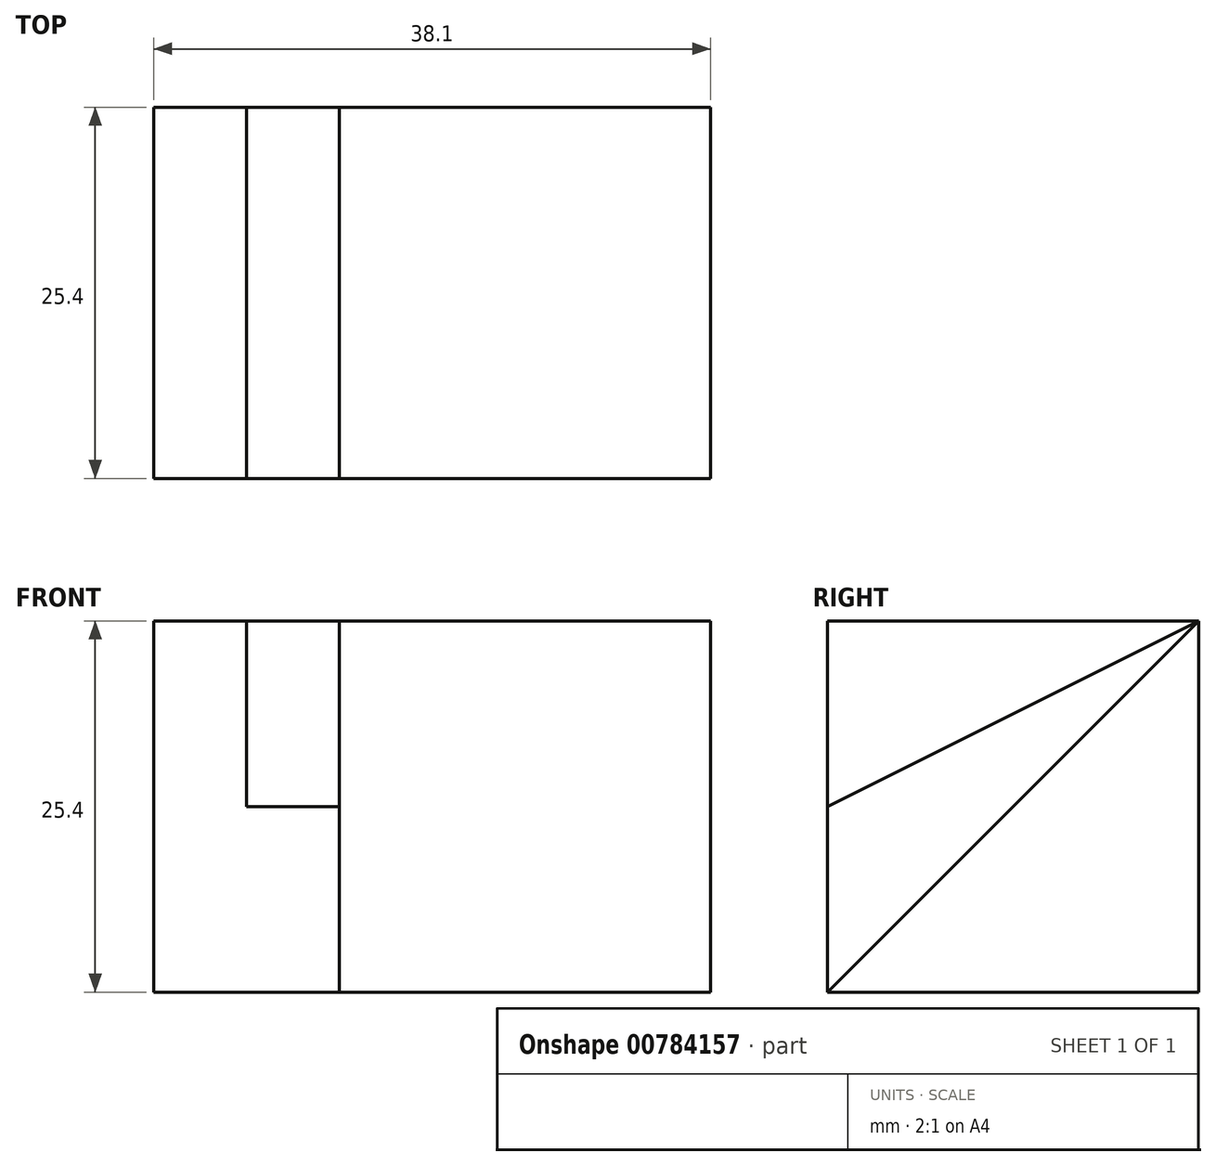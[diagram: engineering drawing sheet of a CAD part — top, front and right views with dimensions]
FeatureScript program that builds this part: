
annotation { "Feature Type Name" : "Feature", "Feature Type Description" : "" }
export const myFeature = defineFeature(function(context is Context, id is Id, definition is map)
    precondition{}
    {
        {
            var Q0;
            Q0=qCreatedBy(makeId("Front.planeOp"),FACE);
            var sketch = newSketch(context, id + "F0", { "sketchPlane" : qUnion([Q0])});
            skLineSegment(sketch, "E0", {"start": v(0, 0) * mm, "end": v(38.1, 0) * mm});
            skLineSegment(sketch, "E1", {"start": v(38.1, 0) * mm, "end": v(38.1, 25.4) * mm});
            skLineSegment(sketch, "E2", {"start": v(38.1, 25.4) * mm, "end": v(0, 25.4) * mm});
            skLineSegment(sketch, "E3", {"start": v(0, 25.4) * mm, "end": v(0, 0) * mm});
            skSolve(sketch);
        }
        {
            var Q0;
            Q0=makeQuery(id+"F0.imprint","IMPRINT",FACE,{"disambiguationData":[TD([[makeQuery(id+"F0.imprint","IMPRINT",EDGE,{"derivedFrom":sQuery(id+"F0.wireOp",EDGE,"E0")}),1.0]])]});
            extrude(context, id + "F1", {"entities" : qUnion([Q0]), "depth" : 25.4 * mm, "offsetDistance" : 25.4 * mm});
        }
        {
            var Q0;
            Q0=makeQuery(id+"F1.opExtrude","SWEPT_FACE",FACE,{"disambiguationData":[OSD([sQuery(id+"F0.wireOp",EDGE,"E1")])]});
            var sketch = newSketch(context, id + "F2", { "sketchPlane" : qUnion([Q0])});
            skLineSegment(sketch, "E4", {"start": v(0, 25.4) * mm, "end": v(-25.4, 0) * mm});
            skSolve(sketch);
        }
        {
            var Q0;
            Q0=makeQuery(id+"F2.imprint","IMPRINT",FACE,{"disambiguationData":[TD([[makeQuery(id+"F2.imprint","IMPRINT",EDGE,{"derivedFrom":sQuery(id+"F2.wireOp",EDGE,"E4")}),-1.0]])]});
            extrude(context, id + "F3", {"entities" : qUnion([Q0]), "operationType" : NewBodyOperationType.REMOVE, "oppositeDirection" : true, "depth" : 25.4 * mm, "offsetDistance" : 25.4 * mm});
        }
        {
            var Q0;
            Q0=makeQuery(id+"F1.opExtrude","CAP_FACE",FACE,{"disambiguationData":[OSD([sQuery(id+"F0.wireOp",EDGE,"E0"),sQuery(id+"F0.wireOp",EDGE,"E1"),sQuery(id+"F0.wireOp",EDGE,"E2"),sQuery(id+"F0.wireOp",EDGE,"E3")])],"isStart":false});
            var sketch = newSketch(context, id + "F4", { "sketchPlane" : qUnion([Q0])});
            skLineSegment(sketch, "E5", {"start": v(12.7, 0) * mm, "end": v(12.7, 12.7) * mm});
            skLineSegment(sketch, "E6", {"start": v(12.7, 12.7) * mm, "end": v(37.77, 50.75) * mm});
            skLineSegment(sketch, "E7", {"start": v(37.77, 50.75) * mm, "end": v(12.7, 25.4) * mm});
            skLineSegment(sketch, "E8", {"start": v(12.7, 25.4) * mm, "end": v(12.7, 12.7) * mm});
            skSolve(sketch);
        }
        {
            var Q0;
            Q0=makeQuery(id+"F4.imprint","IMPRINT",FACE,{"disambiguationData":[TD([[makeQuery(id+"F4.imprint","IMPRINT",EDGE,{"derivedFrom":sQuery(id+"F4.wireOp",EDGE,"E6")}),1.0]])]});
            extrude(context, id + "F5", {"entities" : qUnion([Q0]), "operationType" : NewBodyOperationType.REMOVE, "oppositeDirection" : true, "depth" : 12.7 * mm, "offsetDistance" : 25.4 * mm});
        }
        {
            var Q0;
            Q0=makeQuery(id+"F3.boolean.opBoolean","COPY",FACE,{"derivedFrom":makeQuery(id+"F3.opExtrude","CAP_FACE",FACE,{"disambiguationData":[OSD([sQuery(id+"F0.wireOp",EDGE,"E1"),sQuery(id+"F0.wireOp",EDGE,"E2"),sQuery(id+"F2.wireOp",EDGE,"E4")])],"isStart":false})});
            var sketch = newSketch(context, id + "F6", { "sketchPlane" : qUnion([Q0])});
            skLineSegment(sketch, "E9", {"start": v(-25.4, 0) * mm, "end": v(-25.4, 12.7) * mm});
            skLineSegment(sketch, "E10", {"start": v(-25.4, 12.7) * mm, "end": v(0, 25.4) * mm});
            skSolve(sketch);
        }
        {
            var Q0;
            {var subQ0=sQuery(id+"F6.wireOp",EDGE,"E10");Q0=makeQuery(id+"F6.imprint","IMPRINT",FACE,{"disambiguationData":[TD([[makeQuery(id+"F6.imprint","IMPRINT",EDGE,{"derivedFrom":subQ0}),1.0]])]});}
            extrude(context, id + "F7", {"entities" : qUnion([Q0]), "operationType" : NewBodyOperationType.REMOVE, "oppositeDirection" : true, "depth" : 6.35 * mm, "offsetDistance" : 25.4 * mm});
        }
    });
